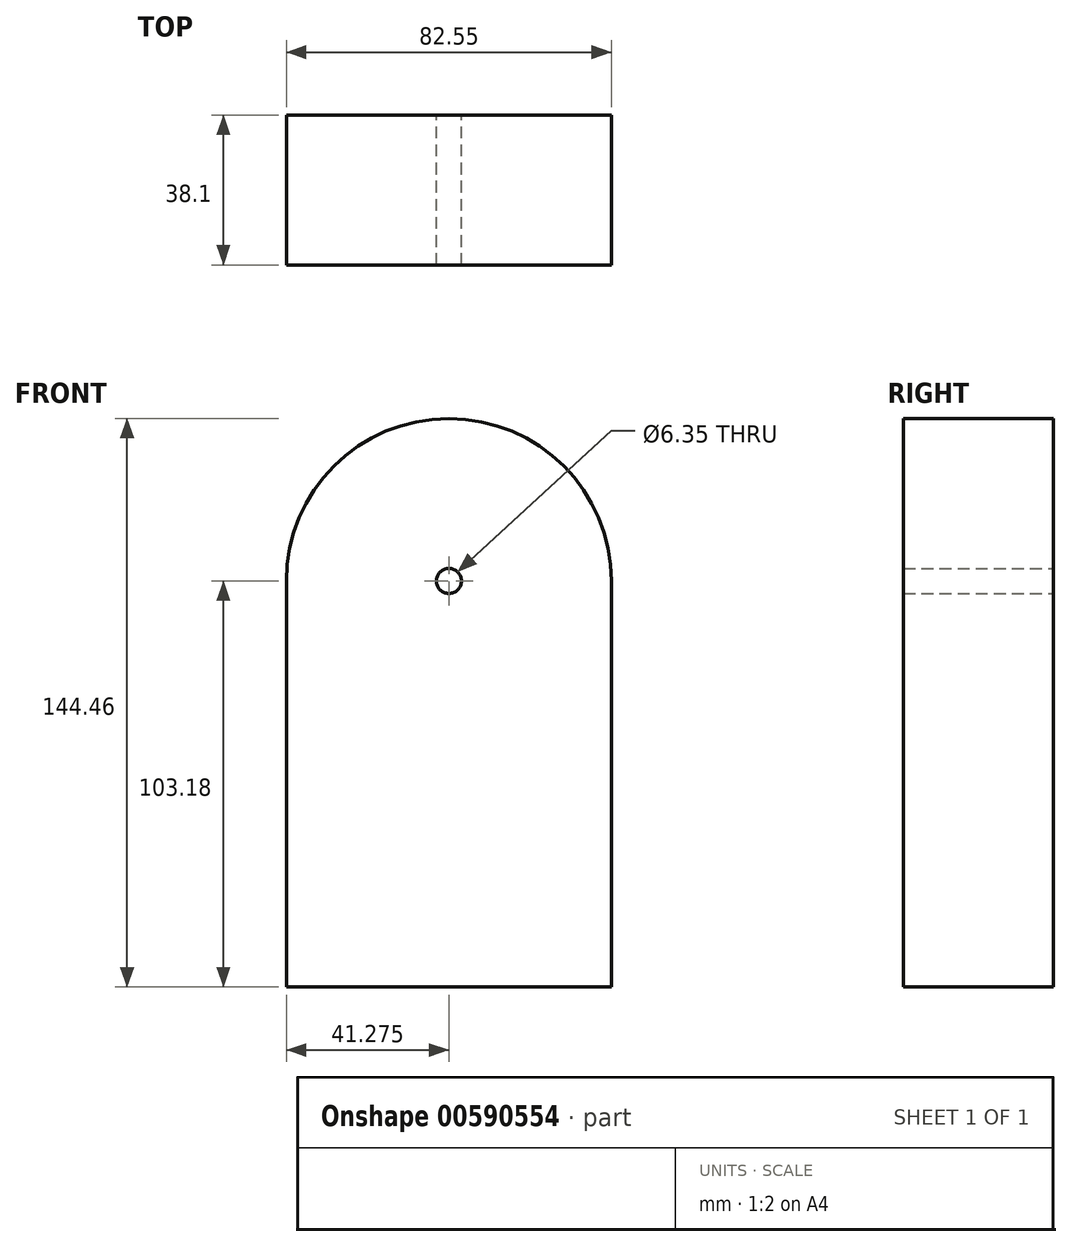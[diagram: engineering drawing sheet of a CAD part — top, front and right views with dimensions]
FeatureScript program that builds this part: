
annotation { "Feature Type Name" : "Feature", "Feature Type Description" : "" }
export const myFeature = defineFeature(function(context is Context, id is Id, definition is map)
    precondition{}
    {
        {
            var Q0;
            Q0=qCreatedBy(makeId("Front.planeOp"),FACE);
            var sketch = newSketch(context, id + "F0", { "sketchPlane" : qUnion([Q0])});
            skLineSegment(sketch, "E0", {"start": v(0, 0) * mm, "end": v(0, -103.18) * mm});
            skLineSegment(sketch, "E1", {"start": v(0, -103.18) * mm, "end": v(-82.55, -103.18) * mm});
            skLineSegment(sketch, "E2", {"start": v(-82.55, -103.18) * mm, "end": v(-82.55, 0) * mm});
            skLineSegment(sketch, "E3", {"start": v(-82.55, 0) * mm, "end": v(0, 0) * mm, "construction": true});
            skArc(sketch, "E4", {"start": v(0, 0) * mm, "mid": v(-41.28, 41.28) * mm, "end": v(-82.55, 0) * mm});
            skCircle(sketch, "E5", {"center": v(-41.28, 0) * mm, "radius": 3.18 * mm});
            skSolve(sketch);
        }
        {
            var Q0;
            Q0=makeQuery(id+"F0.imprint","IMPRINT",FACE,{"disambiguationData":[TD([[makeQuery(id+"F0.imprint","IMPRINT",EDGE,{"derivedFrom":sQuery(id+"F0.wireOp",EDGE,"E0")}),-1.0]])]});
            extrude(context, id + "F1", {"entities" : qUnion([Q0]), "depth" : 38.1 * mm, "offsetDistance" : 25.4 * mm});
        }
    });
